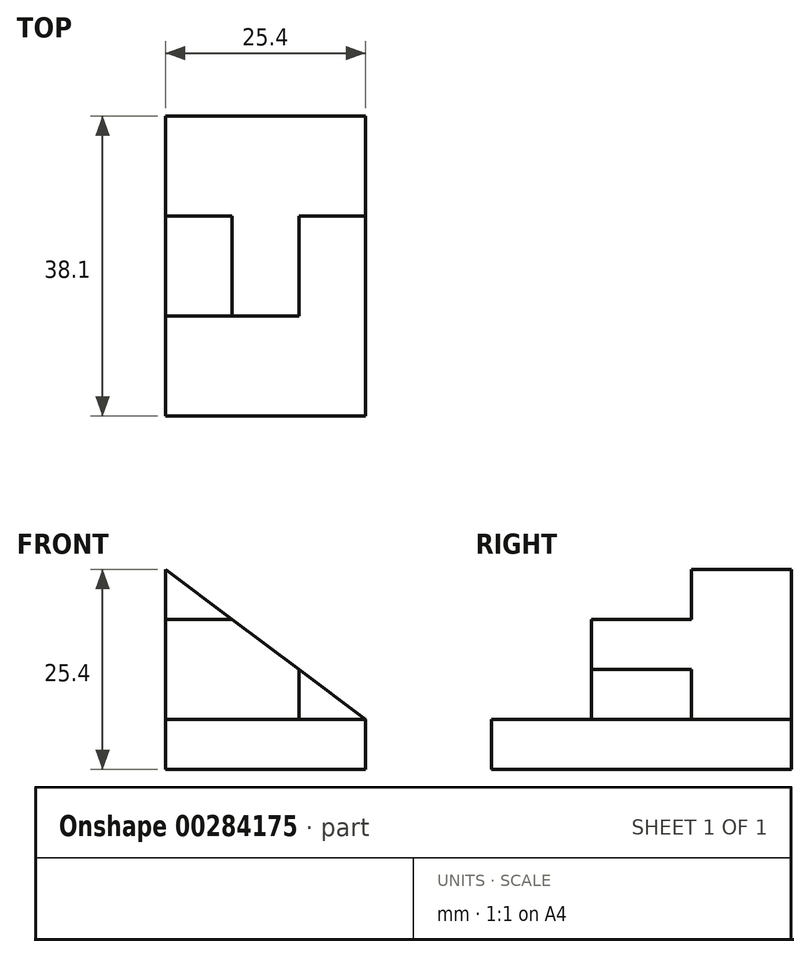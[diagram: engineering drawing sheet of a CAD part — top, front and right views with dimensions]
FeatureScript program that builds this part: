
annotation { "Feature Type Name" : "Feature", "Feature Type Description" : "" }
export const myFeature = defineFeature(function(context is Context, id is Id, definition is map)
    precondition{}
    {
        {
            var Q0;
            Q0=qCreatedBy(makeId("Front.planeOp"),FACE);
            var sketch = newSketch(context, id + "F0", { "sketchPlane" : qUnion([Q0])});
            skLineSegment(sketch, "E0", {"start": v(0, 6.35) * mm, "end": v(0, 0) * mm});
            skLineSegment(sketch, "E1", {"start": v(0, 0) * mm, "end": v(25.4, 0) * mm});
            skLineSegment(sketch, "E2", {"start": v(25.4, 0) * mm, "end": v(25.4, 6.35) * mm});
            skLineSegment(sketch, "E3", {"start": v(25.4, 6.35) * mm, "end": v(0, 6.35) * mm});
            skSolve(sketch);
        }
        {
            var Q0;
            Q0 = qSketchRegion(id + "F0", true);
            extrude(context, id + "F1", {"entities" : qUnion([Q0]), "depth" : 38.1 * mm});
        }
        {
            var Q0;
            Q0=qCreatedBy(makeId("Front.planeOp"),FACE);
            var sketch = newSketch(context, id + "F2", { "sketchPlane" : qUnion([Q0])});
            skLineSegment(sketch, "E4", {"start": v(0, 6.35) * mm, "end": v(25.4, 6.35) * mm});
            skLineSegment(sketch, "E5", {"start": v(25.4, 6.35) * mm, "end": v(25.4, 25.4) * mm});
            skLineSegment(sketch, "E6", {"start": v(25.4, 25.4) * mm, "end": v(0, 25.4) * mm});
            skLineSegment(sketch, "E7", {"start": v(0, 25.4) * mm, "end": v(0, 6.35) * mm});
            skSolve(sketch);
        }
        {
            var Q0;
            Q0 = qSketchRegion(id + "F2", true);
            extrude(context, id + "F3", {"entities" : qUnion([Q0]), "operationType" : NewBodyOperationType.ADD, "depth" : 12.7 * mm});
        }
        {
            var Q0;
            Q0=qCreatedBy(makeId("Front.planeOp"),FACE);
            var sketch = newSketch(context, id + "F4", { "sketchPlane" : qUnion([Q0])});
            skLineSegment(sketch, "E8.bottom", {"start": v(0, 19.05) * mm, "end": v(16.94, 19.05) * mm});
            skLineSegment(sketch, "E8.top", {"start": v(0, 6.35) * mm, "end": v(16.94, 6.35) * mm});
            skLineSegment(sketch, "E8.left", {"start": v(0, 19.05) * mm, "end": v(0, 6.35) * mm});
            skLineSegment(sketch, "E8.right", {"start": v(16.94, 19.05) * mm, "end": v(16.94, 6.35) * mm});
            skSolve(sketch);
        }
        {
            var Q0;
            Q0 = qSketchRegion(id + "F4", true);
            extrude(context, id + "F5", {"entities" : qUnion([Q0]), "operationType" : NewBodyOperationType.ADD, "depth" : 25.4 * mm});
        }
        {
            var Q0;
            Q0=qCreatedBy(makeId("Front.planeOp"),FACE);
            var sketch = newSketch(context, id + "F6", { "sketchPlane" : qUnion([Q0])});
            skLineSegment(sketch, "E9", {"start": v(0, 25.4) * mm, "end": v(25.4, 6.35) * mm});
            skLineSegment(sketch, "E10", {"start": v(25.4, 6.35) * mm, "end": v(25.4, 25.4) * mm});
            skLineSegment(sketch, "E11", {"start": v(25.4, 25.4) * mm, "end": v(0, 25.4) * mm});
            skSolve(sketch);
        }
        {
            var Q0;
            Q0 = qSketchRegion(id + "F6", true);
            extrude(context, id + "F7", {"entities" : qUnion([Q0]), "operationType" : NewBodyOperationType.REMOVE, "depth" : 25.4 * mm});
        }
    });
